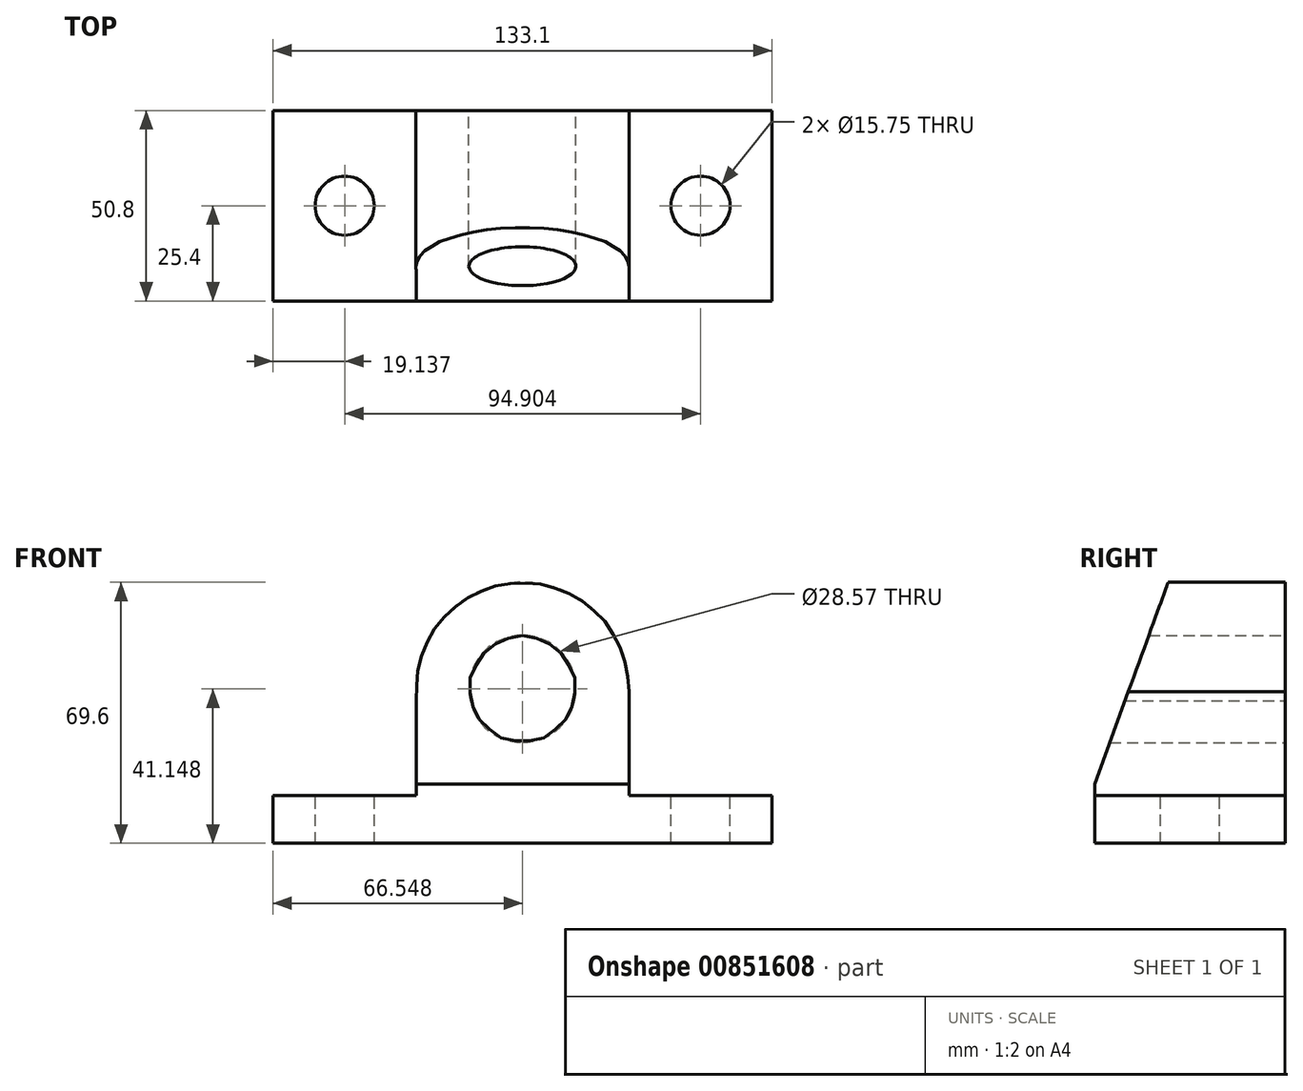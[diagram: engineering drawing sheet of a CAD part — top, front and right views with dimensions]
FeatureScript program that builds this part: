
annotation { "Feature Type Name" : "Feature", "Feature Type Description" : "" }
export const myFeature = defineFeature(function(context is Context, id is Id, definition is map)
    precondition{}
    {
        {
            var Q0;
            Q0=qCreatedBy(makeId("Front.planeOp"),FACE);
            var sketch = newSketch(context, id + "F0", { "sketchPlane" : qUnion([Q0])});
            skLineSegment(sketch, "E0.bottom", {"start": v(0, 0) * mm, "end": v(133.1, 0) * mm});
            skLineSegment(sketch, "E0.top", {"start": v(0, 12.7) * mm, "end": v(38.27, 12.7) * mm});
            skLineSegment(sketch, "E0.left", {"start": v(0, 0) * mm, "end": v(0, 12.7) * mm});
            skLineSegment(sketch, "E0.right", {"start": v(133.1, 0) * mm, "end": v(133.1, 12.7) * mm});
            skCircle(sketch, "E1", {"center": v(66.55, 41.15) * mm, "radius": 14.29 * mm});
            skArc(sketch, "E2", {"start": v(94.99, 40.4) * mm, "mid": v(65.35, 69.57) * mm, "end": v(38.27, 38) * mm});
            skLineSegment(sketch, "E3", {"start": v(38.27, 44.3) * mm, "end": v(38.27, 12.7) * mm});
            skLineSegment(sketch, "E4", {"start": v(94.99, 41.9) * mm, "end": v(94.99, 12.7) * mm});
            skLineSegment(sketch, "E5", {"start": v(38.27, 12.7) * mm, "end": v(38.27, 15.75) * mm});
            skLineSegment(sketch, "E6", {"start": v(38.27, 15.75) * mm, "end": v(94.99, 15.75) * mm});
            skLineSegment(sketch, "E7.trimOffspring", {"start": v(94.99, 12.7) * mm, "end": v(133.1, 12.7) * mm});
            skSolve(sketch);
        }
        {
            var Q0;
            Q0 = qSketchRegion(id + "F0", true);
            extrude(context, id + "F1", {"entities" : qUnion([Q0]), "depth" : 50.8 * mm, "offsetDistance" : 25.4 * mm});
        }
        {
            var Q0;
            Q0=makeQuery(id+"F1.opExtrude","SWEPT_FACE",FACE,{"disambiguationData":[OSD([sQuery(id+"F0.wireOp",EDGE,"E0.top")])]});
            var sketch = newSketch(context, id + "F2", { "sketchPlane" : qUnion([Q0])});
            skCircle(sketch, "E8", {"center": v(19.14, -25.4) * mm, "radius": 7.87 * mm});
            skSolve(sketch);
        }
        {
            var Q0;
            Q0=makeQuery(id+"F1.opExtrude","SWEPT_FACE",FACE,{"disambiguationData":[OSD([sQuery(id+"F0.wireOp",EDGE,"E7.trimOffspring")])]});
            var sketch = newSketch(context, id + "F3", { "sketchPlane" : qUnion([Q0])});
            skCircle(sketch, "E9", {"center": v(114.04, -25.4) * mm, "radius": 7.87 * mm});
            skSolve(sketch);
        }
        {
            var Q0;
            Q0=makeQuery(id+"F3.imprint","IMPRINT",FACE,{"disambiguationData":[TD([[makeQuery(id+"F3.imprint","IMPRINT",EDGE,{"derivedFrom":sQuery(id+"F3.wireOp",EDGE,"E9")}),1.0]])]});
            var Q1;
            Q1=makeQuery(id+"F2.imprint","IMPRINT",FACE,{"disambiguationData":[TD([[makeQuery(id+"F2.imprint","IMPRINT",EDGE,{"derivedFrom":sQuery(id+"F2.wireOp",EDGE,"E8")}),1.0]])]});
            extrude(context, id + "F4", {"entities" : qUnion([Q0, Q1]), "operationType" : NewBodyOperationType.REMOVE, "oppositeDirection" : true, "depth" : 25.4 * mm, "offsetDistance" : 25.4 * mm});
        }
        {
            var Q0;
            Q0=makeQuery(id+"F1.opExtrude","SWEPT_FACE",FACE,{"disambiguationData":[OSD([sQuery(id+"F0.wireOp",EDGE,"E4")])]});
            var sketch = newSketch(context, id + "F5", { "sketchPlane" : qUnion([Q0])});
            skLineSegment(sketch, "E10", {"start": v(-50.8, 12.7) * mm, "end": v(-50.8, 15.75) * mm});
            skLineSegment(sketch, "E11", {"start": v(-50.8, 15.75) * mm, "end": v(-50.8, 68.64) * mm});
            skLineSegment(sketch, "E12", {"start": v(-50.8, 15.75) * mm, "end": v(-30, 72.9) * mm});
            skLineSegment(sketch, "E13", {"start": v(-30, 72.9) * mm, "end": v(-51.09, 72.9) * mm});
            skLineSegment(sketch, "E14", {"start": v(-51.09, 72.9) * mm, "end": v(-50.8, 68.64) * mm});
            skSolve(sketch);
        }
        {
            var Q0;
            Q0 = qSketchRegion(id + "F5", true);
            extrude(context, id + "F6", {"entities" : qUnion([Q0]), "operationType" : NewBodyOperationType.REMOVE, "oppositeDirection" : true, "depth" : 127 * mm, "offsetDistance" : 25.4 * mm});
        }
        {
            var Q0;
            Q0=makeQuery(id+"F6.boolean.opBoolean","COPY",FACE,{"derivedFrom":makeQuery(id+"F6.opExtrude","CAP_FACE",FACE,{"disambiguationData":[OSD([sQuery(id+"F5.wireOp",EDGE,"E11"),sQuery(id+"F5.wireOp",EDGE,"E12"),sQuery(id+"F5.wireOp",EDGE,"E13"),sQuery(id+"F5.wireOp",EDGE,"E14")])],"isStart":true})});
            var sketch = newSketch(context, id + "F7", { "sketchPlane" : qUnion([Q0])});
            skLineSegment(sketch, "E15", {"start": v(50.8, 41.9) * mm, "end": v(41.28, 41.9) * mm});
            skLineSegment(sketch, "E16", {"start": v(41.28, 41.9) * mm, "end": v(41.83, 40.4) * mm});
            skLineSegment(sketch, "E17", {"start": v(41.83, 40.4) * mm, "end": v(50.8, 40.4) * mm});
            skLineSegment(sketch, "E18", {"start": v(50.8, 40.4) * mm, "end": v(50.8, 41.9) * mm});
            skSolve(sketch);
        }
        {
            var Q0;
            Q0=makeQuery(id+"F7.imprint","IMPRINT",FACE,{"disambiguationData":[TD([[makeQuery(id+"F7.imprint","IMPRINT",EDGE,{"derivedFrom":sQuery(id+"F7.wireOp",EDGE,"E15")}),-1.0]])]});
            extrude(context, id + "F8", {"entities" : qUnion([Q0]), "operationType" : NewBodyOperationType.REMOVE, "oppositeDirection" : true, "depth" : 25.4 * mm, "offsetDistance" : 25.4 * mm});
        }
    });
